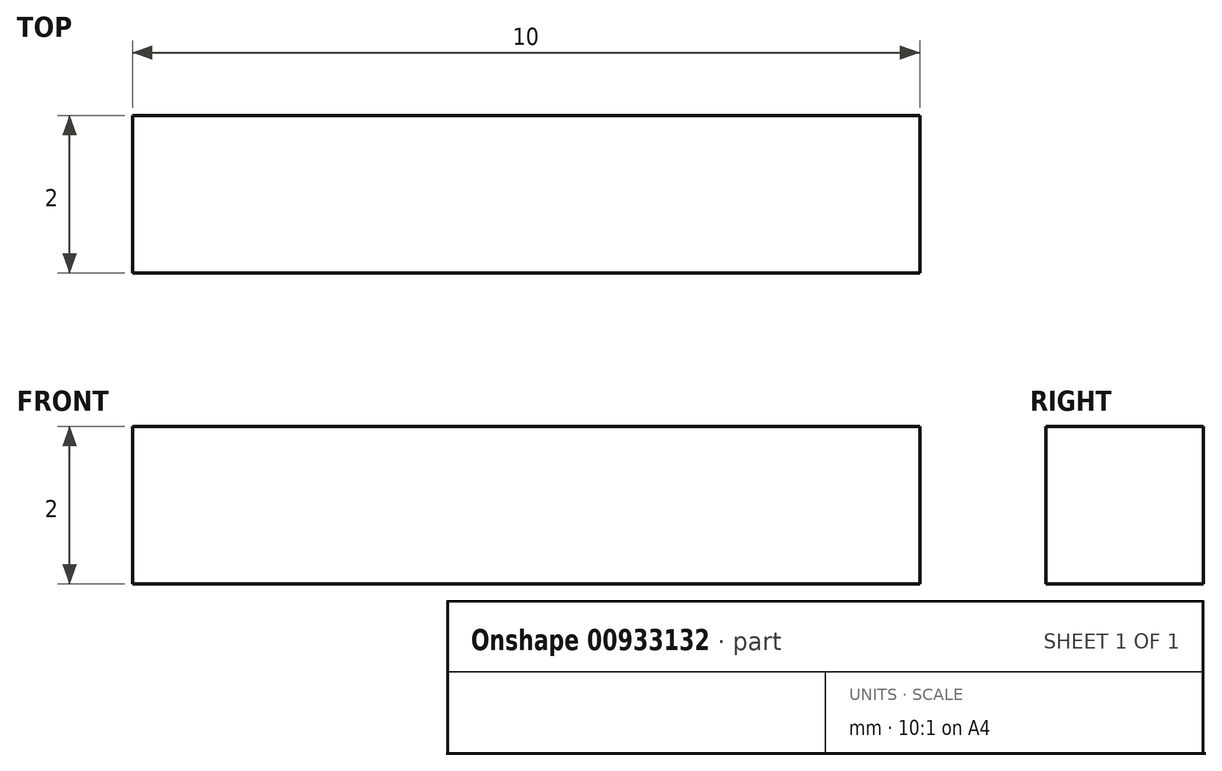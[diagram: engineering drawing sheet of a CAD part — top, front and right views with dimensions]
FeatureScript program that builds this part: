
annotation { "Feature Type Name" : "Feature", "Feature Type Description" : "" }
export const myFeature = defineFeature(function(context is Context, id is Id, definition is map)
    precondition{}
    {
        {
            var Q0;
            Q0=qCreatedBy(makeId("Top.planeOp"),FACE);
            var sketch = newSketch(context, id + "F0", { "sketchPlane" : qUnion([Q0])});
            skLineSegment(sketch, "E0.bottom", {"start": v(-5.38, 0) * mm, "end": v(4.62, 0) * mm});
            skLineSegment(sketch, "E0.top", {"start": v(-5.38, 2) * mm, "end": v(4.62, 2) * mm});
            skLineSegment(sketch, "E0.left", {"start": v(-5.38, 0) * mm, "end": v(-5.38, 2) * mm});
            skLineSegment(sketch, "E0.right", {"start": v(4.62, 0) * mm, "end": v(4.62, 2) * mm});
            skSolve(sketch);
        }
        {
            var Q0;
            Q0=makeQuery(id+"F0.imprint","IMPRINT",FACE,{"disambiguationData":[TD([[makeQuery(id+"F0.imprint","IMPRINT",EDGE,{"derivedFrom":sQuery(id+"F0.wireOp",EDGE,"E0.bottom")}),1.0]])]});
            extrude(context, id + "F1", {"entities" : qUnion([Q0]), "depth" : 2 * mm, "offsetDistance" : 25 * mm});
        }
    });
